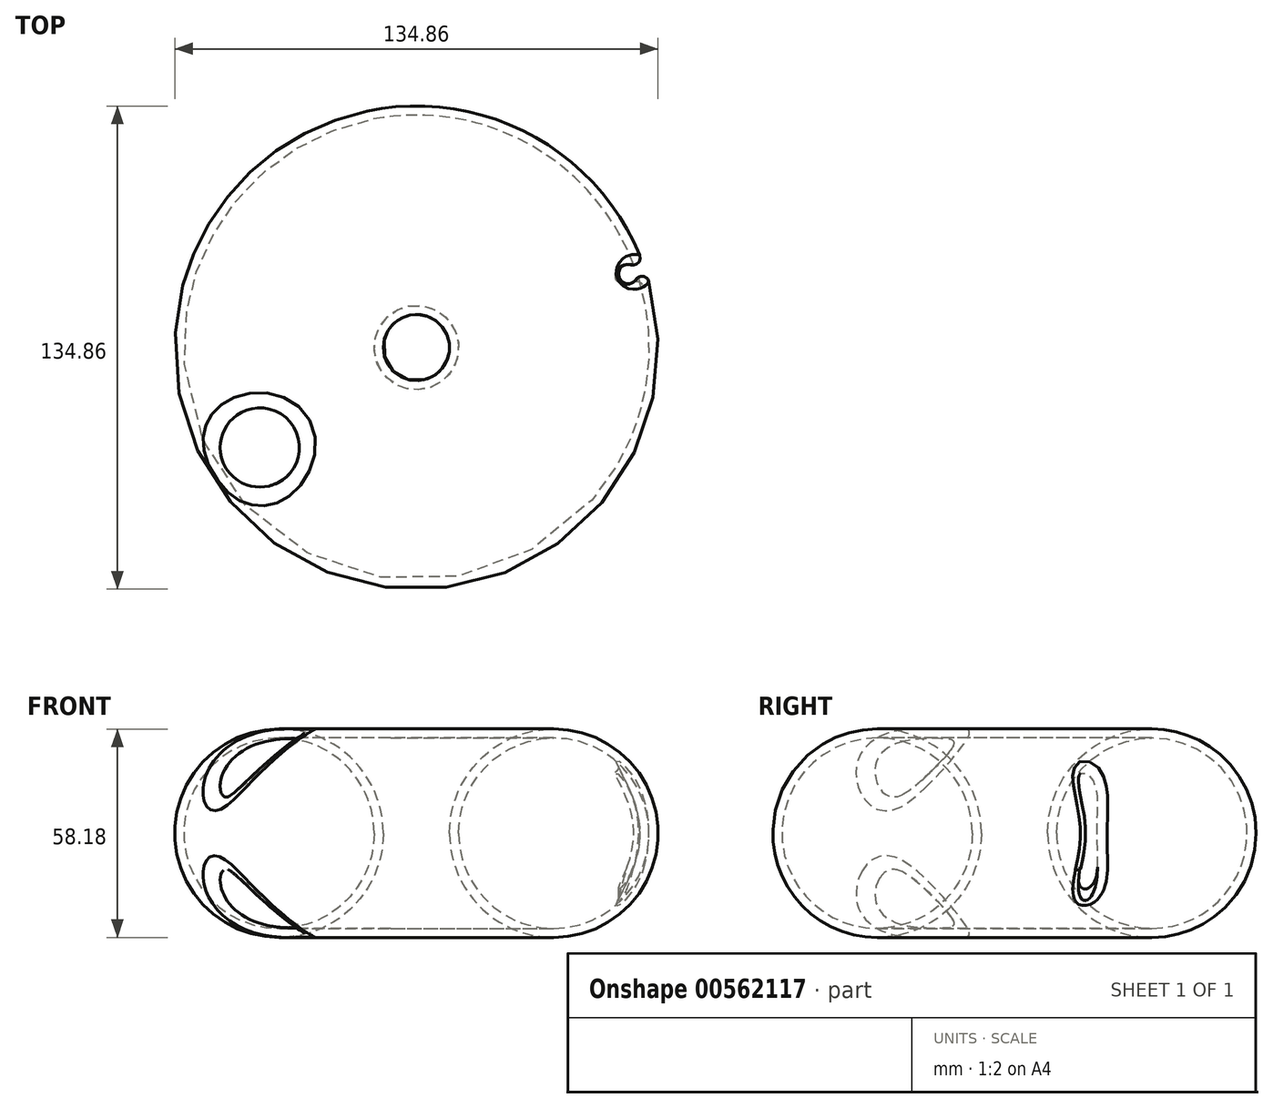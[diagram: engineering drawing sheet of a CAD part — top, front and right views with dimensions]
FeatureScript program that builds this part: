
annotation { "Feature Type Name" : "Feature", "Feature Type Description" : "" }
export const myFeature = defineFeature(function(context is Context, id is Id, definition is map)
    precondition{}
    {
        {
            var Q0;
            Q0=qCreatedBy(makeId("Front.planeOp"),FACE);
            var sketch = newSketch(context, id + "F0", { "sketchPlane" : qUnion([Q0])});
            skCircle(sketch, "E0", {"center": v(38.34, 31.8) * mm, "radius": 29.1 * mm});
            skLineSegment(sketch, "E1", {"start": v(0, 0) * mm, "end": v(0, 63.17) * mm, "construction": true});
            skSolve(sketch);
        }
        {
            var Q0;
            Q0=makeQuery(id+"F0.imprint","IMPRINT",FACE,{"disambiguationData":[TD([[makeQuery(id+"F0.imprint","IMPRINT",EDGE,{"derivedFrom":sQuery(id+"F0.wireOp",EDGE,"E0")}),1.0]])]});
            var Q1;
            Q1=sQuery(id+"F0.wireOp",EDGE,"E1");
            revolve(context, id + "F1", {"entities" : qUnion([Q0]), "axis" : qUnion([Q1]), "revolveType" : RevolveType.FULL});
        }
        {
            var Q0;
            Q0=qCreatedBy(makeId("Top.planeOp"),FACE);
            var sketch = newSketch(context, id + "F2", { "sketchPlane" : qUnion([Q0])});
            skCircle(sketch, "E2", {"center": v(-43.7, -27.87) * mm, "radius": 11.06 * mm});
            skSolve(sketch);
        }
        {
            var Q0;
            Q0 = qSketchRegion(id + "F2", true);
            extrude(context, id + "F3", {"entities" : qUnion([Q0]), "operationType" : NewBodyOperationType.REMOVE, "depth" : 118.87 * mm, "offsetDistance" : 25.4 * mm});
        }
        {
            var Q0;
            Q0=makeQuery(id+"F3.boolean.opBoolean","COPY",FACE,{"derivedFrom":makeQuery(id+"F3.opExtrude","SWEPT_FACE",FACE,{"disambiguationData":[OSD([sQuery(id+"F2.wireOp",EDGE,"E2")])]})});
            shell(context, id + "F4", {"entities" : qUnion([Q0]), "thickness" : 2.54 * mm});
        }
        {
            var Q0;
            Q0=qCreatedBy(makeId("Top.planeOp"),FACE);
            var sketch = newSketch(context, id + "F5", { "sketchPlane" : qUnion([Q0])});
            skCircle(sketch, "E3", {"center": v(59.05, 20.53) * mm, "radius": 2.68 * mm});
            skSolve(sketch);
        }
        {
            var Q0;
            Q0 = qSketchRegion(id + "F5", true);
            extrude(context, id + "F6", {"entities" : qUnion([Q0]), "operationType" : NewBodyOperationType.REMOVE, "depth" : 23.1 * mm, "offsetDistance" : 25.4 * mm});
        }
        {
            var Q0;
            Q0=makeQuery(id+"F3.boolean.opBoolean","INTERSECT",EDGE,{"disambiguationData":[OD(1.0)],"derivedFrom":[makeQuery(id+"F1.opRevolve","SWEPT_FACE",FACE,{"disambiguationData":[OSD([sQuery(id+"F0.wireOp",EDGE,"E0")])]}),makeQuery(id+"F3.opExtrude","SWEPT_FACE",FACE,{"disambiguationData":[OSD([sQuery(id+"F2.wireOp",EDGE,"E2")])]})]});
            var Q1;
            Q1=makeQuery(id+"F3.boolean.opBoolean","INTERSECT",EDGE,{"disambiguationData":[OD(0.0)],"derivedFrom":[makeQuery(id+"F1.opRevolve","SWEPT_FACE",FACE,{"disambiguationData":[OSD([sQuery(id+"F0.wireOp",EDGE,"E0")])]}),makeQuery(id+"F3.opExtrude","SWEPT_FACE",FACE,{"disambiguationData":[OSD([sQuery(id+"F2.wireOp",EDGE,"E2")])]})]});
            fillet(context, id + "F7", {"entities" : qUnion([Q0, Q1]), "radius" : 5.08 * mm, "tangentPropagation" : true, "allowEdgeOverflow" : false});
        }
        {
            var Q0;
            Q0=makeQuery(id+"F6.boolean.opBoolean","INTERSECT",EDGE,{"derivedFrom":[makeQuery(id+"F1.opRevolve","SWEPT_FACE",FACE,{"disambiguationData":[OSD([sQuery(id+"F0.wireOp",EDGE,"E0")])]}),makeQuery(id+"F6.opExtrude","SWEPT_FACE",FACE,{"disambiguationData":[OSD([sQuery(id+"F5.wireOp",EDGE,"E3")])]})]});
            fillet(context, id + "F8", {"entities" : qUnion([Q0]), "radius" : 2.03 * mm, "tangentPropagation" : true, "allowEdgeOverflow" : false});
        }
    });
